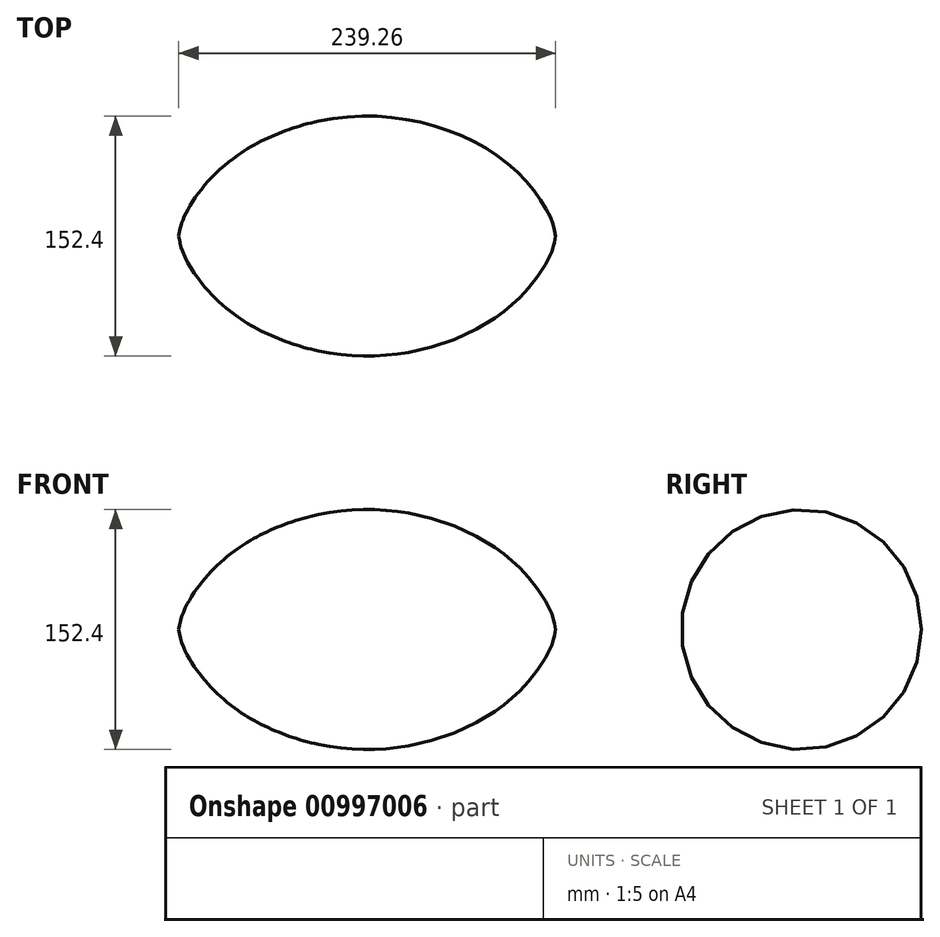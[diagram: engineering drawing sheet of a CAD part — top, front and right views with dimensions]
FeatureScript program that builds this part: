
annotation { "Feature Type Name" : "Feature", "Feature Type Description" : "" }
export const myFeature = defineFeature(function(context is Context, id is Id, definition is map)
    precondition{}
    {
        {
            var Q0;
            Q0=qCreatedBy(makeId("Top.planeOp"),FACE);
            var sketch = newSketch(context, id + "F0", { "sketchPlane" : qUnion([Q0])});
            skLineSegment(sketch, "E0", {"start": v(-317.78, 0) * mm, "end": v(250.62, 0) * mm});
            skCircle(sketch, "E1", {"center": v(-46.32, 38.1) * mm, "radius": 38.1 * mm});
            skPoint(sketch, "E2", {"position": v(119.63, 0) * mm});
            skPoint(sketch, "E3", {"position": v(-129.5, 0) * mm});
            skLineSegment(sketch, "E4", {"start": v(0, 0) * mm, "end": v(-28.8, 23.7) * mm, "construction": true});
            skPoint(sketch, "E5", {"position": v(0, 76.2) * mm});
            skPoint(sketch, "E6", {"position": v(56.85, 65.04) * mm});
            skPoint(sketch, "E7", {"position": v(97.92, 38.1) * mm});
            skPoint(sketch, "E8", {"position": v(116.67, 11.16) * mm});
            skLineSegment(sketch, "E9", {"start": v(0, 0) * mm, "end": v(0, -40.58) * mm, "construction": true});
            skPoint(sketch, "E10.MirrorP", {"position": v(-119.63, 0) * mm});
            skPoint(sketch, "E11.MirrorP", {"position": v(-116.67, 11.16) * mm});
            skPoint(sketch, "E12.MirrorP", {"position": v(-97.92, 38.1) * mm});
            skPoint(sketch, "E13.MirrorP", {"position": v(-56.85, 65.04) * mm});
            skFitSpline(sketch, "E14", {"points": [v(119.63, 0) * mm, v(116.67, 11.16) * mm, v(97.92, 38.1) * mm, v(56.85, 65.04) * mm, v(0, 76.2) * mm, v(-56.85, 65.04) * mm, v(-97.92, 38.1) * mm, v(-116.67, 11.16) * mm, v(-119.63, 0) * mm], "startDerivative": vector(-23.6, 141.45) * mm, "endDerivative": vector(-23.6, -141.45) * mm});
            skSolve(sketch);
        }
        {
            var Q0;
            {var subQ0=sQuery(id+"F0.wireOp",EDGE,"E14");var subQ1=sQuery(id+"F0.wireOp",EDGE,"E0");var subQ2=makeQuery(id+"F0.imprint","INTERSECT",VERTEX,{"disambiguationData":[OD(0.0)],"derivedFrom":[subQ1,subQ0]});Q0=makeQuery(id+"F0.imprint","IMPRINT",FACE,{"disambiguationData":[TD([[makeQuery(id+"F0.imprint","IMPRINT",EDGE,{"disambiguationData":[TD([[subQ2,1.0]])],"derivedFrom":subQ1}),1.0]])]});}
            var Q1;
            {var subQ0=sQuery(id+"F0.wireOp",EDGE,"E1");var subQ1=makeQuery(id+"F0.imprint","INTERSECT",VERTEX,{"derivedFrom":[sQuery(id+"F0.wireOp",EDGE,"E0"),subQ0]});Q1=makeQuery(id+"F0.imprint","IMPRINT",FACE,{"disambiguationData":[TD([[makeQuery(id+"F0.imprint","IMPRINT",EDGE,{"disambiguationData":[TD([[subQ1,1.0]])],"derivedFrom":subQ0}),1.0]])]});}
            var Q2;
            {var subQ0=sQuery(id+"F0.wireOp",EDGE,"E14");var subQ1=sQuery(id+"F0.wireOp",EDGE,"E0");var subQ2=makeQuery(id+"F0.imprint","INTERSECT",VERTEX,{"disambiguationData":[OD(1.0)],"derivedFrom":[subQ1,subQ0]});Q2=makeQuery(id+"F0.imprint","IMPRINT",FACE,{"disambiguationData":[TD([[makeQuery(id+"F0.imprint","IMPRINT",EDGE,{"disambiguationData":[TD([[subQ2,-1.0]])],"derivedFrom":subQ1}),1.0]])]});}
            var Q3;
            Q3=sQuery(id+"F0.wireOp",EDGE,"E0");
            revolve(context, id + "F1", {"surfaceOperationType" : NewSurfaceOperationType.NEW, "entities" : qUnion([Q0, Q1, Q2]), "axis" : qUnion([Q3]), "revolveType" : RevolveType.FULL});
        }
    });
